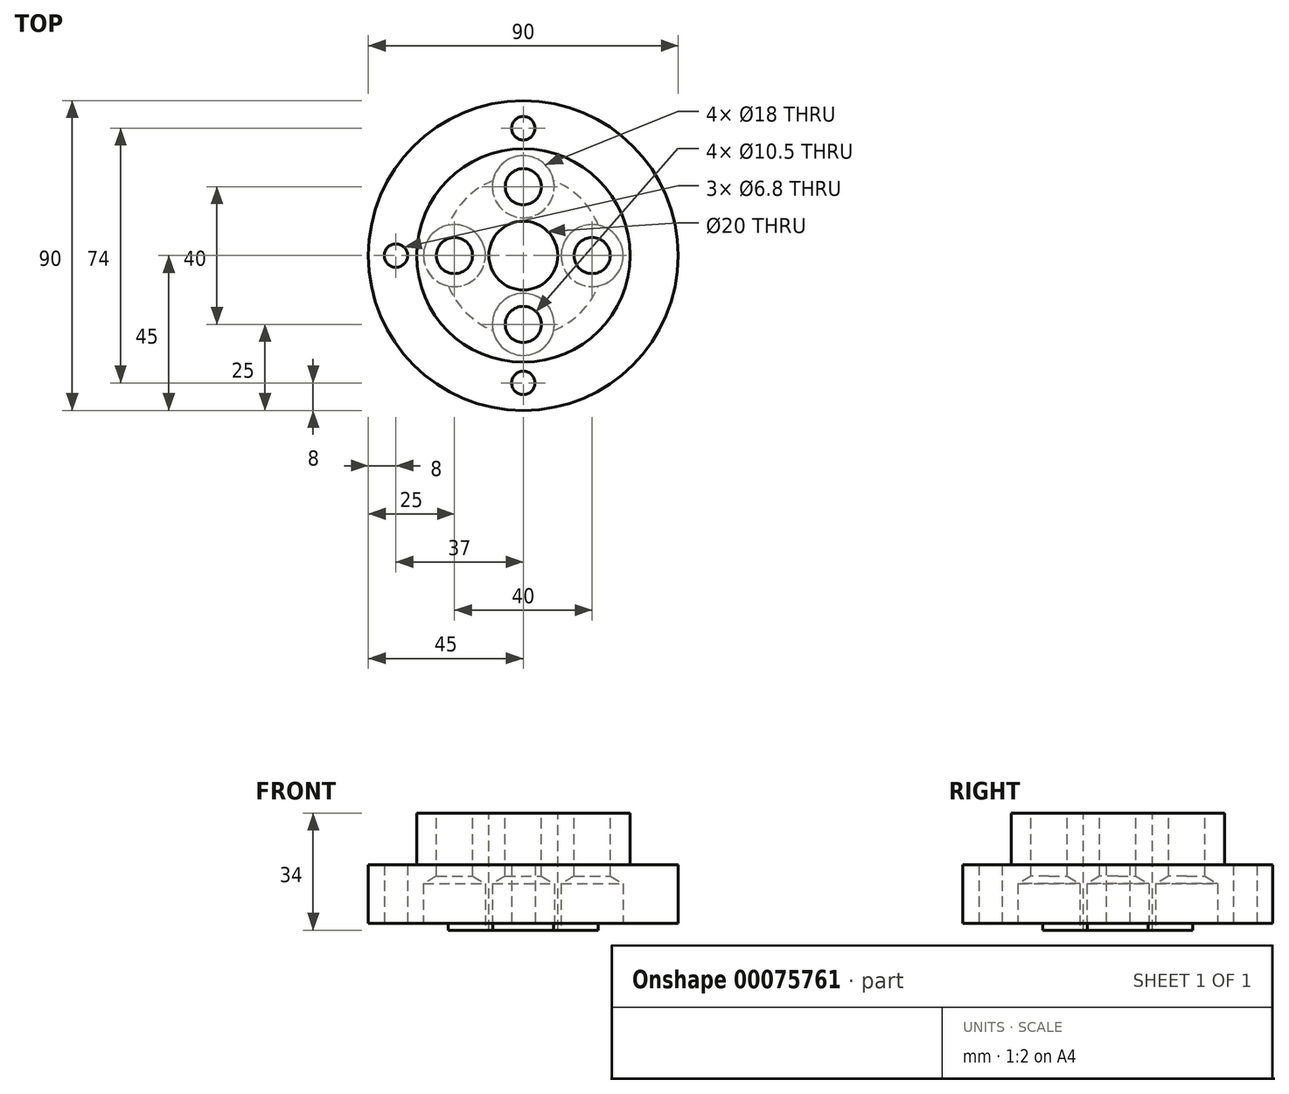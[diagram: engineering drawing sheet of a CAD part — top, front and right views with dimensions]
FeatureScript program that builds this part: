
annotation { "Feature Type Name" : "Feature", "Feature Type Description" : "" }
export const myFeature = defineFeature(function(context is Context, id is Id, definition is map)
    precondition{}
    {
        {
            var Q0;
            Q0=qCreatedBy(makeId("Top.planeOp"),FACE);
            var sketch = newSketch(context, id + "F0", { "sketchPlane" : qUnion([Q0])});
            skCircle(sketch, "E0", {"center": v(0, 0) * mm, "radius": 45 * mm});
            skSolve(sketch);
        }
        {
            var Q0;
            Q0 = qSketchRegion(id + "F0", true);
            extrude(context, id + "F1", {"entities" : qUnion([Q0]), "depth" : 17 * mm});
        }
        {
            var Q0;
            Q0=makeQuery(id+"F1.opExtrude","CAP_FACE",FACE,{"disambiguationData":[OSD([sQuery(id+"F0.wireOp",EDGE,"E0")])],"isStart":false});
            var sketch = newSketch(context, id + "F2", { "sketchPlane" : qUnion([Q0])});
            skCircle(sketch, "E1", {"center": v(0, 0) * mm, "radius": 31 * mm});
            skSolve(sketch);
        }
        {
            var Q0;
            Q0 = qSketchRegion(id + "F2", true);
            extrude(context, id + "F3", {"entities" : qUnion([Q0]), "operationType" : NewBodyOperationType.ADD, "depth" : 15 * mm});
        }
        {
            var Q0;
            Q0=makeQuery(id+"F3.opExtrude","CAP_FACE",FACE,{"disambiguationData":[OSD([sQuery(id+"F2.wireOp",EDGE,"E1")])],"isStart":false});
            var sketch = newSketch(context, id + "F4", { "sketchPlane" : qUnion([Q0])});
            skCircle(sketch, "E2", {"center": v(0, 0) * mm, "radius": 10 * mm});
            skSolve(sketch);
        }
        {
            var Q0;
            Q0=makeQuery(id+"F3.opExtrude","CAP_FACE",FACE,{"disambiguationData":[OSD([sQuery(id+"F2.wireOp",EDGE,"E1")])],"isStart":false});
            var sketch = newSketch(context, id + "F5", { "sketchPlane" : qUnion([Q0])});
            skCircle(sketch, "E3", {"center": v(20, 0) * mm, "radius": 5.25 * mm});
            skCircle(sketch, "E4", {"center": v(0, -20) * mm, "radius": 5.25 * mm});
            skCircle(sketch, "E5", {"center": v(-20, 0) * mm, "radius": 5.25 * mm});
            skCircle(sketch, "E6", {"center": v(0, 20) * mm, "radius": 5.25 * mm});
            skSolve(sketch);
        }
        {
            var Q0;
            Q0=makeQuery(id+"F1.opExtrude","CAP_FACE",FACE,{"disambiguationData":[OSD([sQuery(id+"F0.wireOp",EDGE,"E0")])],"isStart":true});
            var sketch = newSketch(context, id + "F6", { "sketchPlane" : qUnion([Q0])});
            skCircle(sketch, "E7", {"center": v(0, 0) * mm, "radius": 23.5 * mm});
            skSolve(sketch);
        }
        {
            var Q0;
            Q0 = qSketchRegion(id + "F6", true);
            extrude(context, id + "F7", {"entities" : qUnion([Q0]), "operationType" : NewBodyOperationType.ADD, "depth" : 2 * mm});
        }
        {
            var Q0;
            Q0=makeQuery(id+"F7.opExtrude","CAP_FACE",FACE,{"disambiguationData":[OSD([sQuery(id+"F6.wireOp",EDGE,"E7")])],"isStart":false});
            var sketch = newSketch(context, id + "F8", { "sketchPlane" : qUnion([Q0])});
            skCircle(sketch, "E8", {"center": v(0, 20) * mm, "radius": 9 * mm});
            skCircle(sketch, "E9", {"center": v(20, 0) * mm, "radius": 9 * mm});
            skCircle(sketch, "E10", {"center": v(0, -20) * mm, "radius": 9 * mm});
            skCircle(sketch, "E11", {"center": v(-20, 0) * mm, "radius": 9 * mm});
            skSolve(sketch);
        }
        {
            var Q0;
            Q0=sQuery(id+"F8.wireOp",VERTEX,"E11.center");
            var Q1;
            Q1=sQuery(id+"F8.wireOp",VERTEX,"E8.center");
            var Q2;
            Q2=sQuery(id+"F8.wireOp",VERTEX,"E9.center");
            var Q3;
            Q3=sQuery(id+"F8.wireOp",VERTEX,"E10.center");
            var Q4;
            Q4=makeQuery(id+"F1.opExtrude","SWEPT_BODY",BODY,{"disambiguationData":[OSD([sQuery(id+"F0.wireOp",EDGE,"E0")])]});
            hole(context, id + "F9", {"style" : HoleStyle.SIMPLE, "endStyle" : HoleEndStyle.BLIND, "holeDiameter" : 18 * mm, "holeDepth" : 13.5 * mm, "startFromSketch" : true, "locations" : qUnion([Q0, Q1, Q2, Q3]), "scope" : qUnion([Q4])});
        }
        {
            var Q0;
            Q0=sQuery(id+"F4.wireOp",VERTEX,"E2.center");
            var Q1;
            Q1=makeQuery(id+"F1.opExtrude","SWEPT_BODY",BODY,{"disambiguationData":[OSD([sQuery(id+"F0.wireOp",EDGE,"E0")])]});
            hole(context, id + "F10", {"style" : HoleStyle.SIMPLE, "endStyle" : HoleEndStyle.THROUGH, "holeDiameter" : 20 * mm, "startFromSketch" : true, "locations" : qUnion([Q0]), "scope" : qUnion([Q1]), "isTappedThrough" : true});
        }
        {
            var Q0;
            Q0=sQuery(id+"F5.wireOp",VERTEX,"E5.center");
            var Q1;
            Q1=sQuery(id+"F5.wireOp",VERTEX,"E6.center");
            var Q2;
            Q2=sQuery(id+"F5.wireOp",VERTEX,"E3.center");
            var Q3;
            Q3=sQuery(id+"F5.wireOp",VERTEX,"E4.center");
            var Q4;
            Q4=makeQuery(id+"F1.opExtrude","SWEPT_BODY",BODY,{"disambiguationData":[OSD([sQuery(id+"F0.wireOp",EDGE,"E0")])]});
            hole(context, id + "F11", {"style" : HoleStyle.SIMPLE, "endStyle" : HoleEndStyle.THROUGH, "holeDiameter" : 10.5 * mm, "startFromSketch" : true, "locations" : qUnion([Q0, Q1, Q2, Q3]), "scope" : qUnion([Q4]), "isTappedThrough" : true});
        }
        {
            var Q0;
            Q0=makeQuery(id+"F1.opExtrude","CAP_FACE",FACE,{"disambiguationData":[OSD([sQuery(id+"F0.wireOp",EDGE,"E0")])],"isStart":true});
            var sketch = newSketch(context, id + "F12", { "sketchPlane" : qUnion([Q0])});
            skLineSegment(sketch, "E12", {"start": v(0, 0) * mm, "end": v(-37, 0) * mm});
            skLineSegment(sketch, "E13", {"start": v(0, 0) * mm, "end": v(0, 37) * mm});
            skPoint(sketch, "E13.endSnap0", {"position": v(0, 29) * mm});
            skLineSegment(sketch, "E14.MirrorCS", {"start": v(0, 0) * mm, "end": v(37, 0) * mm});
            skLineSegment(sketch, "E15.MirrorCS", {"start": v(0, 0) * mm, "end": v(0, -37) * mm});
            skSolve(sketch);
        }
        {
            var Q0;
            Q0=sQuery(id+"F12.wireOp",VERTEX,"E13.end");
            var Q1;
            Q1=sQuery(id+"F12.wireOp",VERTEX,"E12.end");
            var Q2;
            Q2=sQuery(id+"F12.wireOp",VERTEX,"E15.MirrorCS.end");
            var Q3;
            Q3=sQuery(id+"F12.wireOp",VERTEX,"E14.MirrorCS.end");
            var Q4;
            Q4=makeQuery(id+"F1.opExtrude","SWEPT_BODY",BODY,{"disambiguationData":[OSD([sQuery(id+"F0.wireOp",EDGE,"E0")])]});
            hole(context, id + "F13", {"style" : HoleStyle.SIMPLE, "endStyle" : HoleEndStyle.THROUGH, "holeDiameter" : 6.8 * mm, "startFromSketch" : true, "locations" : qUnion([Q0, Q1, Q2, Q3]), "scope" : qUnion([Q4]), "isTappedThrough" : true});
        }
    });
